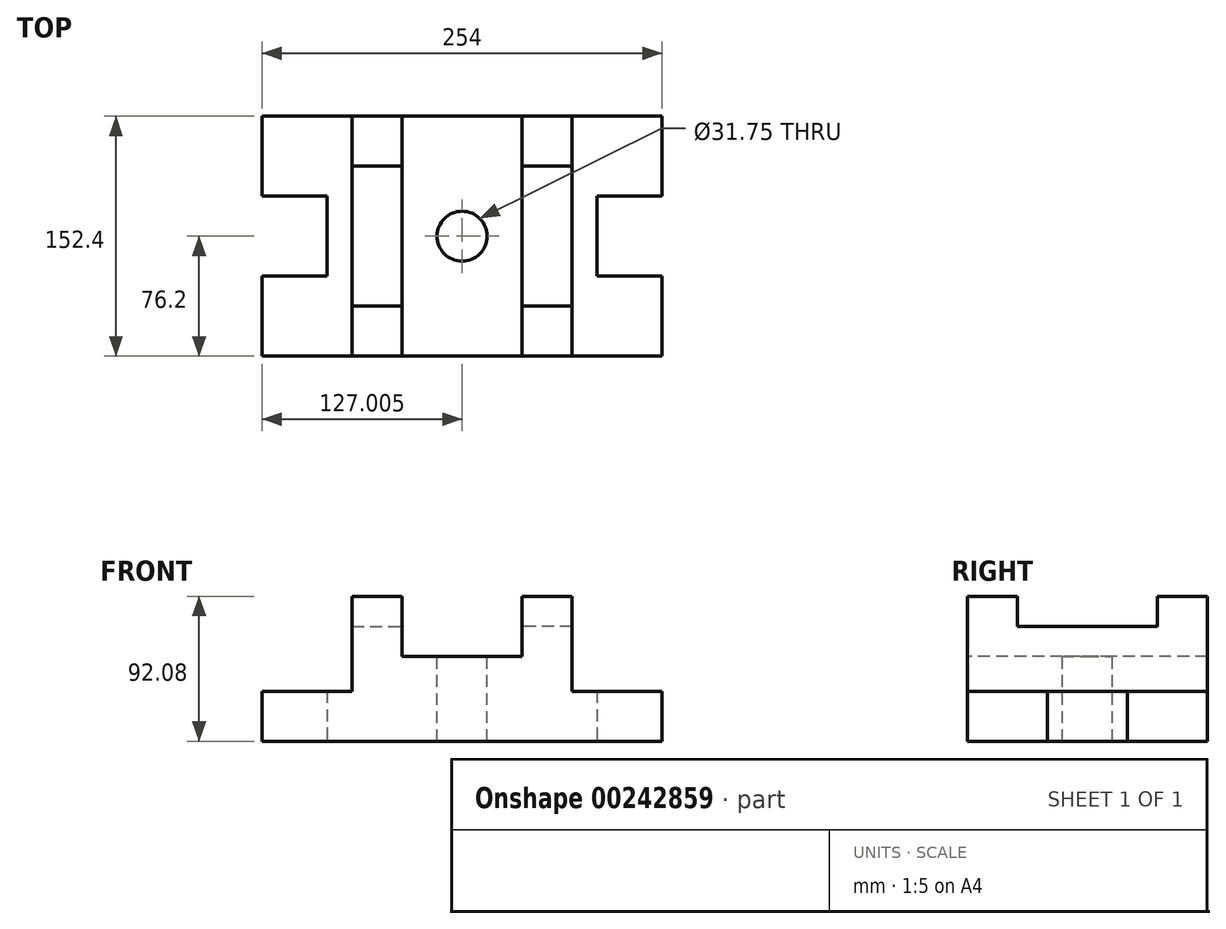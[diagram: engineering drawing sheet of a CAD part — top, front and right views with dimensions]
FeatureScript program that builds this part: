
annotation { "Feature Type Name" : "Feature", "Feature Type Description" : "" }
export const myFeature = defineFeature(function(context is Context, id is Id, definition is map)
    precondition{}
    {
        {
            var Q0;
            Q0=qCreatedBy(makeId("Top.planeOp"),FACE);
            var sketch = newSketch(context, id + "F0", { "sketchPlane" : qUnion([Q0])});
            skLineSegment(sketch, "E0", {"start": v(-136.53, -76.2) * mm, "end": v(117.48, -76.2) * mm});
            skLineSegment(sketch, "E1", {"start": v(-136.53, 76.2) * mm, "end": v(117.47, 76.2) * mm});
            skLineSegment(sketch, "E2", {"start": v(117.48, -76.2) * mm, "end": v(117.48, -25.4) * mm});
            skLineSegment(sketch, "E3", {"start": v(-136.53, -76.2) * mm, "end": v(-136.53, -25.4) * mm});
            skLineSegment(sketch, "E4", {"start": v(-136.53, -25.4) * mm, "end": v(-95.25, -25.4) * mm});
            skLineSegment(sketch, "E5", {"start": v(-95.25, -25.4) * mm, "end": v(-95.25, 25.4) * mm});
            skLineSegment(sketch, "E6", {"start": v(-95.25, 25.4) * mm, "end": v(-136.53, 25.4) * mm});
            skLineSegment(sketch, "E7", {"start": v(-136.53, 25.4) * mm, "end": v(-136.53, 76.2) * mm});
            skLineSegment(sketch, "E8", {"start": v(117.47, -25.4) * mm, "end": v(76.2, -25.4) * mm});
            skLineSegment(sketch, "E9", {"start": v(76.2, -25.4) * mm, "end": v(76.2, 25.4) * mm});
            skLineSegment(sketch, "E10", {"start": v(76.2, 25.4) * mm, "end": v(117.47, 25.4) * mm});
            skLineSegment(sketch, "E11", {"start": v(117.47, 25.4) * mm, "end": v(117.47, 76.2) * mm});
            skSolve(sketch);
        }
        {
            var Q0;
            Q0=makeQuery(id+"F0.imprint","IMPRINT",FACE,{"disambiguationData":[TD([[makeQuery(id+"F0.imprint","IMPRINT",EDGE,{"derivedFrom":sQuery(id+"F0.wireOp",EDGE,"E0")}),1.0]])]});
            extrude(context, id + "F1", {"entities" : qUnion([Q0]), "depth" : 31.75 * mm});
        }
        {
            var Q0;
            Q0=makeQuery(id+"F1.opExtrude","CAP_FACE",FACE,{"disambiguationData":[OSD([sQuery(id+"F0.wireOp",EDGE,"E0"),sQuery(id+"F0.wireOp",EDGE,"E1"),sQuery(id+"F0.wireOp",EDGE,"E2"),sQuery(id+"F0.wireOp",EDGE,"E3"),sQuery(id+"F0.wireOp",EDGE,"E4"),sQuery(id+"F0.wireOp",EDGE,"E5"),sQuery(id+"F0.wireOp",EDGE,"E6"),sQuery(id+"F0.wireOp",EDGE,"E7"),sQuery(id+"F0.wireOp",EDGE,"E8"),sQuery(id+"F0.wireOp",EDGE,"E9"),sQuery(id+"F0.wireOp",EDGE,"E10"),sQuery(id+"F0.wireOp",EDGE,"E11")])],"isStart":false});
            var sketch = newSketch(context, id + "F2", { "sketchPlane" : qUnion([Q0])});
            skLineSegment(sketch, "E12.bottom", {"start": v(-79.38, 76.2) * mm, "end": v(60.32, 76.2) * mm});
            skLineSegment(sketch, "E12.top", {"start": v(-79.38, -76.2) * mm, "end": v(60.33, -76.2) * mm});
            skLineSegment(sketch, "E12.left", {"start": v(-79.38, 76.2) * mm, "end": v(-79.38, -76.2) * mm});
            skLineSegment(sketch, "E12.right", {"start": v(60.32, 76.2) * mm, "end": v(60.33, -76.2) * mm});
            skSolve(sketch);
        }
        {
            var Q0;
            Q0=makeQuery(id+"F2.imprint","IMPRINT",FACE,{"disambiguationData":[TD([[makeQuery(id+"F2.imprint","IMPRINT",EDGE,{"derivedFrom":sQuery(id+"F2.wireOp",EDGE,"E12.bottom")}),-1.0]])]});
            extrude(context, id + "F3", {"entities" : qUnion([Q0]), "operationType" : NewBodyOperationType.ADD, "depth" : 22.22 * mm});
        }
        {
            var Q0;
            Q0=makeQuery(id+"F3.opExtrude","CAP_FACE",FACE,{"disambiguationData":[OSD([sQuery(id+"F2.wireOp",EDGE,"E12.bottom"),sQuery(id+"F2.wireOp",EDGE,"E12.top"),sQuery(id+"F2.wireOp",EDGE,"E12.left"),sQuery(id+"F2.wireOp",EDGE,"E12.right")])],"isStart":false});
            var sketch = newSketch(context, id + "F4", { "sketchPlane" : qUnion([Q0])});
            skLineSegment(sketch, "E13.bottom", {"start": v(-79.38, 76.2) * mm, "end": v(-47.63, 76.2) * mm});
            skLineSegment(sketch, "E13.top", {"start": v(-79.38, -76.2) * mm, "end": v(-47.62, -76.2) * mm});
            skLineSegment(sketch, "E13.left", {"start": v(-79.38, 76.2) * mm, "end": v(-79.38, -76.2) * mm});
            skLineSegment(sketch, "E13.right", {"start": v(-47.63, 76.2) * mm, "end": v(-47.62, -76.2) * mm});
            skLineSegment(sketch, "E14.bottom", {"start": v(28.57, 76.2) * mm, "end": v(60.33, 76.2) * mm});
            skLineSegment(sketch, "E14.top", {"start": v(28.58, -77.36) * mm, "end": v(60.33, -77.36) * mm});
            skLineSegment(sketch, "E14.left", {"start": v(28.57, 76.2) * mm, "end": v(28.58, -77.36) * mm});
            skLineSegment(sketch, "E14.right", {"start": v(60.32, 76.2) * mm, "end": v(60.33, -77.36) * mm});
            skSolve(sketch);
        }
        {
            var Q0;
            Q0=makeQuery(id+"F4.imprint","IMPRINT",FACE,{"disambiguationData":[TD([[makeQuery(id+"F4.imprint","IMPRINT",EDGE,{"derivedFrom":sQuery(id+"F4.wireOp",EDGE,"E13.bottom")}),-1.0]])]});
            var Q1;
            {var subQ0=sQuery(id+"F4.wireOp",EDGE,"E14.bottom");Q1=makeQuery(id+"F4.imprint","IMPRINT",FACE,{"disambiguationData":[TD([[makeQuery(id+"F4.imprint","IMPRINT",EDGE,{"derivedFrom":subQ0}),-1.0]])]});}
            extrude(context, id + "F5", {"entities" : qUnion([Q0, Q1]), "operationType" : NewBodyOperationType.ADD, "depth" : 19.05 * mm});
        }
        {
            var Q0;
            Q0=makeQuery(id+"F5.opExtrude","CAP_FACE",FACE,{"disambiguationData":[OSD([sQuery(id+"F4.wireOp",EDGE,"E13.bottom"),sQuery(id+"F4.wireOp",EDGE,"E13.top"),sQuery(id+"F4.wireOp",EDGE,"E13.left"),sQuery(id+"F4.wireOp",EDGE,"E13.right")])],"isStart":false});
            var sketch = newSketch(context, id + "F6", { "sketchPlane" : qUnion([Q0])});
            skLineSegment(sketch, "E15.bottom", {"start": v(-79.38, 76.2) * mm, "end": v(-47.62, 76.2) * mm});
            skLineSegment(sketch, "E15.top", {"start": v(-79.38, 44.45) * mm, "end": v(-47.62, 44.45) * mm});
            skLineSegment(sketch, "E15.left", {"start": v(-79.38, 76.2) * mm, "end": v(-79.38, 44.45) * mm});
            skLineSegment(sketch, "E15.right", {"start": v(-47.62, 76.2) * mm, "end": v(-47.62, 44.45) * mm});
            skLineSegment(sketch, "E16.bottom", {"start": v(-79.38, -76.2) * mm, "end": v(-47.62, -76.2) * mm});
            skLineSegment(sketch, "E16.top", {"start": v(-79.38, -44.45) * mm, "end": v(-47.62, -44.45) * mm});
            skLineSegment(sketch, "E16.left", {"start": v(-79.38, -76.2) * mm, "end": v(-79.38, -44.45) * mm});
            skLineSegment(sketch, "E16.right", {"start": v(-47.62, -76.2) * mm, "end": v(-47.62, -44.45) * mm});
            skLineSegment(sketch, "E17.bottom", {"start": v(28.57, 76.2) * mm, "end": v(60.33, 76.2) * mm});
            skLineSegment(sketch, "E17.top", {"start": v(28.57, 44.45) * mm, "end": v(60.33, 44.45) * mm});
            skLineSegment(sketch, "E17.left", {"start": v(28.57, 76.2) * mm, "end": v(28.57, 44.45) * mm});
            skLineSegment(sketch, "E17.right", {"start": v(60.33, 76.2) * mm, "end": v(60.33, 44.45) * mm});
            skLineSegment(sketch, "E18.bottom", {"start": v(60.33, -76.2) * mm, "end": v(28.58, -76.2) * mm});
            skLineSegment(sketch, "E18.top", {"start": v(60.33, -44.45) * mm, "end": v(28.58, -44.45) * mm});
            skLineSegment(sketch, "E18.left", {"start": v(60.33, -76.2) * mm, "end": v(60.32, -44.45) * mm});
            skLineSegment(sketch, "E18.right", {"start": v(28.58, -76.2) * mm, "end": v(28.58, -44.45) * mm});
            skSolve(sketch);
        }
        {
            var Q0;
            Q0=makeQuery(id+"F6.imprint","IMPRINT",FACE,{"disambiguationData":[TD([[makeQuery(id+"F6.imprint","IMPRINT",EDGE,{"derivedFrom":sQuery(id+"F6.wireOp",EDGE,"E16.bottom")}),1.0]])]});
            var Q1;
            Q1=makeQuery(id+"F6.imprint","IMPRINT",FACE,{"disambiguationData":[TD([[makeQuery(id+"F6.imprint","IMPRINT",EDGE,{"derivedFrom":sQuery(id+"F6.wireOp",EDGE,"E15.bottom")}),-1.0]])]});
            var Q2;
            Q2=makeQuery(id+"F6.imprint","IMPRINT",FACE,{"disambiguationData":[TD([[makeQuery(id+"F6.imprint","IMPRINT",EDGE,{"derivedFrom":sQuery(id+"F6.wireOp",EDGE,"E17.bottom")}),-1.0]])]});
            var Q3;
            Q3=makeQuery(id+"F6.imprint","IMPRINT",FACE,{"disambiguationData":[TD([[makeQuery(id+"F6.imprint","IMPRINT",EDGE,{"derivedFrom":sQuery(id+"F6.wireOp",EDGE,"E18.bottom")}),-1.0]])]});
            extrude(context, id + "F7", {"entities" : qUnion([Q0, Q1, Q2, Q3]), "operationType" : NewBodyOperationType.ADD, "depth" : 19.05 * mm});
        }
        {
            var Q0;
            Q0=makeQuery(id+"F3.opExtrude","CAP_FACE",FACE,{"disambiguationData":[OSD([sQuery(id+"F2.wireOp",EDGE,"E12.bottom"),sQuery(id+"F2.wireOp",EDGE,"E12.top"),sQuery(id+"F2.wireOp",EDGE,"E12.left"),sQuery(id+"F2.wireOp",EDGE,"E12.right")])],"isStart":false});
            var sketch = newSketch(context, id + "F8", { "sketchPlane" : qUnion([Q0])});
            skCircle(sketch, "E19", {"center": v(-9.52, 0) * mm, "radius": 15.88 * mm});
            skSolve(sketch);
        }
        {
            var Q0;
            Q0=makeQuery(id+"F8.imprint","IMPRINT",FACE,{"disambiguationData":[TD([[makeQuery(id+"F8.imprint","IMPRINT",EDGE,{"derivedFrom":sQuery(id+"F8.wireOp",EDGE,"E19")}),1.0]])]});
            extrude(context, id + "F9", {"entities" : qUnion([Q0]), "operationType" : NewBodyOperationType.REMOVE, "endBound" : BoundingType.THROUGH_ALL, "oppositeDirection" : true, "depth" : 25.4 * mm});
        }
    });
